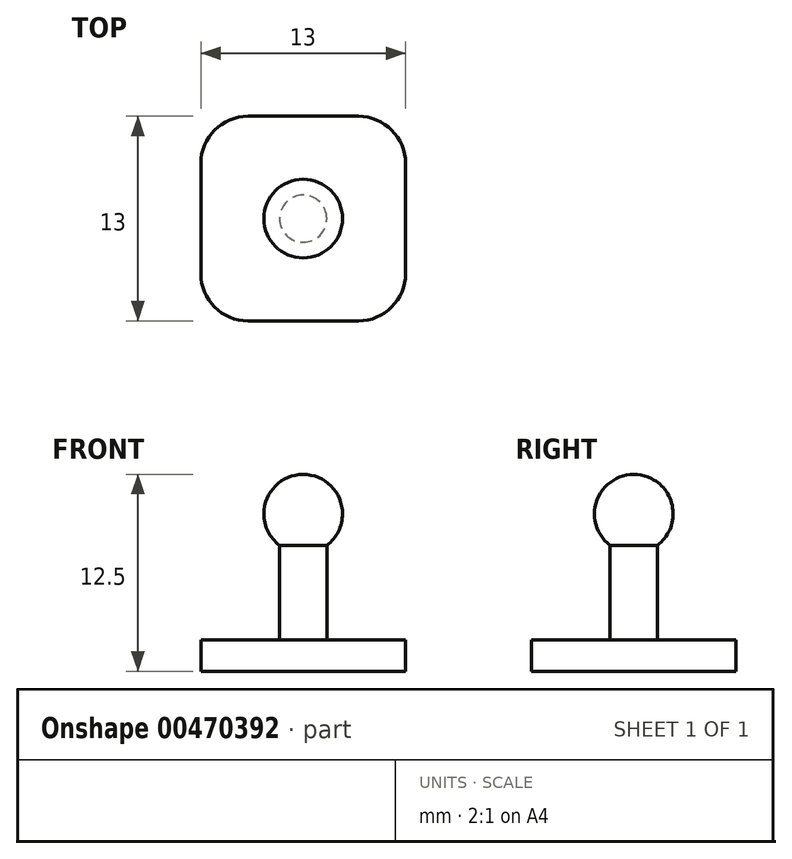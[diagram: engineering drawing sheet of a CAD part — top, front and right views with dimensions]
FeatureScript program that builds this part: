
annotation { "Feature Type Name" : "Feature", "Feature Type Description" : "" }
export const myFeature = defineFeature(function(context is Context, id is Id, definition is map)
    precondition{}
    {
        {
            var Q0;
            Q0=qCreatedBy(makeId("Top.planeOp"),FACE);
            var sketch = newSketch(context, id + "F0", { "sketchPlane" : qUnion([Q0])});
            skLineSegment(sketch, "E0.bottom", {"start": v(3.5, -6.5) * mm, "end": v(-3.5, -6.5) * mm});
            skLineSegment(sketch, "E0.top", {"start": v(3.5, 6.5) * mm, "end": v(-3.5, 6.5) * mm});
            skLineSegment(sketch, "E0.left", {"start": v(6.5, -3.5) * mm, "end": v(6.5, 3.5) * mm});
            skLineSegment(sketch, "E0.right", {"start": v(-6.5, -3.5) * mm, "end": v(-6.5, 3.5) * mm});
            skPoint(sketch, "E0.middle", {"position": v(0, 0) * mm});
            skPoint(sketch, "E1.visualSharp", {"position": v(-6.5, 6.5) * mm});
            skArc(sketch, "E1.filletArc", {"start": v(-3.5, 6.5) * mm, "mid": v(-5.62, 5.62) * mm, "end": v(-6.5, 3.5) * mm});
            skPoint(sketch, "E2.visualSharp", {"position": v(-6.5, -6.5) * mm});
            skArc(sketch, "E2.filletArc", {"start": v(-6.5, -3.5) * mm, "mid": v(-5.62, -5.62) * mm, "end": v(-3.5, -6.5) * mm});
            skPoint(sketch, "E3.visualSharp", {"position": v(6.5, -6.5) * mm});
            skArc(sketch, "E3.filletArc", {"start": v(3.5, -6.5) * mm, "mid": v(5.62, -5.62) * mm, "end": v(6.5, -3.5) * mm});
            skPoint(sketch, "E4.visualSharp", {"position": v(6.5, 6.5) * mm});
            skArc(sketch, "E4.filletArc", {"start": v(6.5, 3.5) * mm, "mid": v(5.62, 5.62) * mm, "end": v(3.5, 6.5) * mm});
            skCircle(sketch, "E5", {"center": v(0, 0) * mm, "radius": 1.5 * mm});
            skSolve(sketch);
        }
        {
            var Q0;
            Q0=makeQuery(id+"F0.imprint","IMPRINT",FACE,{"disambiguationData":[TD([[makeQuery(id+"F0.imprint","IMPRINT",EDGE,{"derivedFrom":sQuery(id+"F0.wireOp",EDGE,"E0.bottom")}),-1.0]])]});
            var Q1;
            Q1=makeQuery(id+"F0.imprint","IMPRINT",FACE,{"disambiguationData":[TD([[makeQuery(id+"F0.imprint","IMPRINT",EDGE,{"derivedFrom":sQuery(id+"F0.wireOp",EDGE,"E5")}),1.0]])]});
            extrude(context, id + "F1", {"entities" : qUnion([Q0, Q1]), "depth" : 2 * mm, "offsetDistance" : 25 * mm});
        }
        {
            var Q0;
            Q0=makeQuery(id+"F0.imprint","IMPRINT",FACE,{"disambiguationData":[TD([[makeQuery(id+"F0.imprint","IMPRINT",EDGE,{"derivedFrom":sQuery(id+"F0.wireOp",EDGE,"E5")}),1.0]])]});
            extrude(context, id + "F2", {"entities" : qUnion([Q0]), "operationType" : NewBodyOperationType.ADD, "depth" : 10 * mm, "offsetDistance" : 25 * mm});
        }
        {
            var Q0;
            Q0=makeQuery(id+"F2.opExtrude","CAP_FACE",FACE,{"disambiguationData":[OSD([sQuery(id+"F0.wireOp",EDGE,"E5")])],"isStart":false});
            var sketch = newSketch(context, id + "F3", { "sketchPlane" : qUnion([Q0])});
            skPoint(sketch, "E6", {"position": v(0, 0) * mm});
            skCircle(sketch, "E7", {"center": v(0, 0) * mm, "radius": 2.5 * mm});
            skSolve(sketch);
        }
        {
            var Q0;
            Q0=qCreatedBy(makeId("Right.planeOp"),FACE);
            var sketch = newSketch(context, id + "F4", { "sketchPlane" : qUnion([Q0])});
            skCircle(sketch, "E8", {"center": v(0, 10) * mm, "radius": 2.5 * mm});
            skSolve(sketch);
        }
        {
            var Q0;
            Q0=makeQuery(id+"F3.imprint","IMPRINT",FACE,{"disambiguationData":[TD([[makeQuery(id+"F3.imprint","IMPRINT",EDGE,{"derivedFrom":makeQuery(id+"F2.opExtrude","CAP_EDGE",EDGE,{"disambiguationData":[OSD([sQuery(id+"F0.wireOp",EDGE,"E5")])],"isStart":false})}),1.0]])]});
            var Q1;
            Q1=makeQuery(id+"F3.imprint","IMPRINT",FACE,{"disambiguationData":[TD([[makeQuery(id+"F3.imprint","IMPRINT",EDGE,{"derivedFrom":sQuery(id+"F3.wireOp",EDGE,"E7")}),1.0]])]});
            var Q2;
            Q2=sQuery(id+"F4.wireOp",EDGE,"E8");
            sweep(context, id + "F5", {"operationType" : NewBodyOperationType.ADD, "profiles" : qUnion([Q0, Q1]), "path" : qUnion([Q2])});
        }
    });
